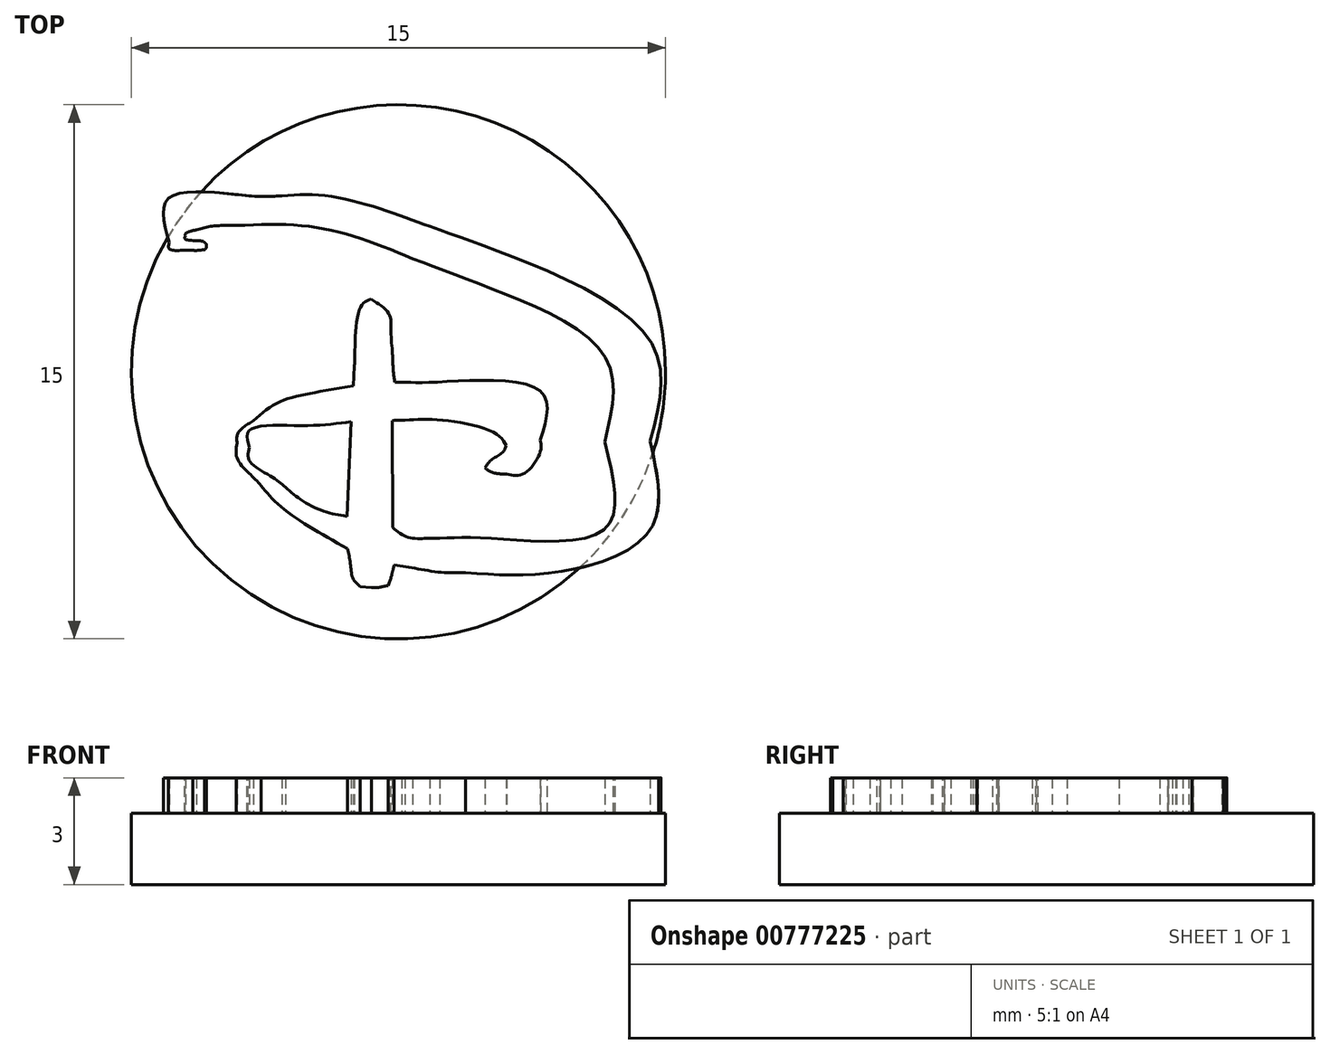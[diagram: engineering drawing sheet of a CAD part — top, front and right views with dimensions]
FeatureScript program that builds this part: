
annotation { "Feature Type Name" : "Feature", "Feature Type Description" : "" }
export const myFeature = defineFeature(function(context is Context, id is Id, definition is map)
    precondition{}
    {
        {
            var Q0;
            Q0=qCreatedBy(makeId("Top.planeOp"),FACE);
            var sketch = newSketch(context, id + "F0", { "sketchPlane" : qUnion([Q0])});
            skCircle(sketch, "E0", {"center": v(0, 0) * mm, "radius": 7.5 * mm});
            skSolve(sketch);
        }
        {
            var Q0;
            Q0=qCreatedBy(makeId("Top.planeOp"),FACE);
            var sketch = newSketch(context, id + "F1", { "sketchPlane" : qUnion([Q0])});
            skFitSpline(sketch, "E1", {"points": [v(-1.32, -1.4) * mm, v(-2.68, -1.51) * mm, v(-4.19, -1.65) * mm, v(-4.19, -2.13) * mm]});
            skFitSpline(sketch, "E2", {"points": [v(-4.19, -2.13) * mm, v(-4.19, -2.5) * mm, v(-3.56, -2.95) * mm, v(-3.17, -3.24) * mm]});
            skFitSpline(sketch, "E3", {"points": [v(-3.17, -3.24) * mm, v(-2.73, -3.6) * mm, v(-2.08, -3.92) * mm, v(-1.45, -4.06) * mm]});
            skFitSpline(sketch, "E4", {"points": [v(-5.78, 3.4) * mm, v(-6.08, 3.4) * mm, v(-6.43, 3.45) * mm, v(-6.43, 3.63) * mm]});
            skFitSpline(sketch, "E5", {"points": [v(-6.43, 3.63) * mm, v(-6.43, 4.89) * mm, v(-4.21, 4.95) * mm, v(-3.27, 4.95) * mm]});
            skFitSpline(sketch, "E6", {"points": [v(-3.27, 4.95) * mm, v(-2.04, 4.95) * mm, v(-0.46, 4.56) * mm, v(0.88, 4.08) * mm]});
            skFitSpline(sketch, "E7", {"points": [v(0.88, 4.08) * mm, v(2.93, 3.34) * mm, v(7.07, 0.87) * mm, v(7.07, -1.95) * mm]});
            skFitSpline(sketch, "E8", {"points": [v(7.07, -1.95) * mm, v(7.07, -4.44) * mm, v(4.38, -5.64) * mm, v(1.88, -5.64) * mm]});
            skFitSpline(sketch, "E9", {"points": [v(1.88, -5.64) * mm, v(1.25, -5.64) * mm, v(0.5, -5.53) * mm, v(-0.12, -5.43) * mm]});
            skFitSpline(sketch, "E10", {"points": [v(-0.12, -5.43) * mm, v(-0.16, -5.58) * mm, v(-0.18, -5.7) * mm, v(-0.28, -6) * mm]});
            skFitSpline(sketch, "E11", {"points": [v(-0.28, -6) * mm, v(-0.45, -6.03) * mm, v(-0.58, -6.06) * mm, v(-0.76, -6.06) * mm]});
            skLineSegment(sketch, "E12", {"start": v(-1.45, -4.06) * mm, "end": v(-1.32, -1.4) * mm});
            skFitSpline(sketch, "E13", {"points": [v(-1.08, -6.03) * mm, v(-1.28, -5.79) * mm, v(-1.35, -5.39) * mm, v(-1.43, -4.96) * mm]});
            skFitSpline(sketch, "E14", {"points": [v(-1.43, -4.96) * mm, v(-2.68, -4.24) * mm, v(-3.49, -3.62) * mm, v(-3.86, -3.2) * mm]});
            skFitSpline(sketch, "E15", {"points": [v(-3.86, -3.2) * mm, v(-4.17, -2.87) * mm, v(-4.53, -2.43) * mm, v(-4.53, -2) * mm]});
            skFitSpline(sketch, "E16", {"points": [v(-4.53, -2) * mm, v(-4.53, -1.78) * mm, v(-4.4, -1.6) * mm, v(-4.08, -1.37) * mm]});
            skFitSpline(sketch, "E17", {"points": [v(-4.08, -1.37) * mm, v(-3.43, -0.9) * mm, v(-2.61, -0.63) * mm, v(-1.27, -0.4) * mm]});
            skLineSegment(sketch, "E18", {"start": v(-0.76, -6.06) * mm, "end": v(-1.08, -6.03) * mm});
            skFitSpline(sketch, "E19", {"points": [v(-1.24, 0.16) * mm, v(-1.23, 0.3) * mm, v(-1.09, 1.77) * mm, v(-0.77, 2.04) * mm]});
            skFitSpline(sketch, "E20", {"points": [v(-0.77, 2.04) * mm, v(-0.27, 1.63) * mm, v(-0.21, 1.2) * mm, v(-0.17, 0.57) * mm]});
            skFitSpline(sketch, "E21", {"points": [v(-0.17, 0.57) * mm, v(-0.16, 0.3) * mm, v(-0.14, 0.01) * mm, v(-0.1, -0.3) * mm]});
            skLineSegment(sketch, "E22", {"start": v(-1.27, -0.4) * mm, "end": v(-1.24, 0.16) * mm});
            skFitSpline(sketch, "E23", {"points": [v(0.09, -0.3) * mm, v(1.05, -0.3) * mm, v(3.98, -0.54) * mm, v(3.98, -1.92) * mm]});
            skFitSpline(sketch, "E24", {"points": [v(3.98, -1.92) * mm, v(3.98, -2.25) * mm, v(3.5, -2.87) * mm, v(3.04, -2.87) * mm]});
            skFitSpline(sketch, "E25", {"points": [v(3.04, -2.87) * mm, v(2.87, -2.87) * mm, v(2.57, -2.8) * mm, v(2.43, -2.69) * mm]});
            skFitSpline(sketch, "E26", {"points": [v(2.43, -2.69) * mm, v(2.64, -2.46) * mm, v(2.94, -2.25) * mm, v(3.02, -2.07) * mm]});
            skFitSpline(sketch, "E27", {"points": [v(3.02, -2.07) * mm, v(2.75, -1.74) * mm, v(1.27, -1.36) * mm, v(0.19, -1.36) * mm]});
            skFitSpline(sketch, "E28", {"points": [v(0.19, -1.36) * mm, v(0, -1.36) * mm, v(-0.06, -1.36) * mm, v(-0.17, -1.37) * mm]});
            skLineSegment(sketch, "E29", {"start": v(-0.1, -0.3) * mm, "end": v(0.09, -0.3) * mm});
            skFitSpline(sketch, "E30", {"points": [v(-0.16, -4.37) * mm, v(0.28, -4.65) * mm, v(0.82, -4.68) * mm, v(1.16, -4.68) * mm]});
            skFitSpline(sketch, "E31", {"points": [v(1.16, -4.68) * mm, v(2.67, -4.68) * mm, v(5.8, -4.42) * mm, v(5.8, -1.98) * mm]});
            skFitSpline(sketch, "E32", {"points": [v(5.8, -1.98) * mm, v(5.8, 0.44) * mm, v(2.7, 2.3) * mm, v(0.4, 3.18) * mm]});
            skFitSpline(sketch, "E33", {"points": [v(0.4, 3.18) * mm, v(-1.21, 3.8) * mm, v(-2.75, 4.1) * mm, v(-4.54, 4.1) * mm]});
            skFitSpline(sketch, "E34", {"points": [v(-4.54, 4.1) * mm, v(-4.91, 4.1) * mm, v(-5.3, 4.08) * mm, v(-5.67, 3.99) * mm]});
            skFitSpline(sketch, "E35", {"points": [v(-5.67, 3.99) * mm, v(-5.9, 3.93) * mm, v(-5.98, 3.88) * mm, v(-5.98, 3.82) * mm]});
            skFitSpline(sketch, "E36", {"points": [v(-5.98, 3.82) * mm, v(-5.98, 3.73) * mm, v(-5.52, 3.67) * mm, v(-5.46, 3.64) * mm]});
            skFitSpline(sketch, "E37", {"points": [v(-5.46, 3.64) * mm, v(-5.42, 3.62) * mm, v(-5.4, 3.57) * mm, v(-5.4, 3.53) * mm]});
            skFitSpline(sketch, "E38", {"points": [v(-5.4, 3.53) * mm, v(-5.4, 3.5) * mm, v(-5.4, 3.46) * mm, v(-5.45, 3.42) * mm]});
            skFitSpline(sketch, "E39", {"points": [v(-5.45, 3.42) * mm, v(-5.5, 3.42) * mm, v(-5.63, 3.4) * mm, v(-5.78, 3.4) * mm]});
            skLineSegment(sketch, "E40", {"start": v(-0.17, -1.37) * mm, "end": v(-0.16, -4.37) * mm});
            skSolve(sketch);
        }
        {
            var Q0;
            Q0 = qSketchRegion(id + "F1", true);
            extrude(context, id + "F2", {"entities" : qUnion([Q0]), "depth" : 1 * mm, "offsetDistance" : 25 * mm});
        }
        {
            var Q0;
            Q0 = qSketchRegion(id + "F0", true);
            extrude(context, id + "F3", {"entities" : qUnion([Q0]), "operationType" : NewBodyOperationType.ADD, "oppositeDirection" : true, "depth" : 2 * mm, "offsetDistance" : 25 * mm});
        }
    });
